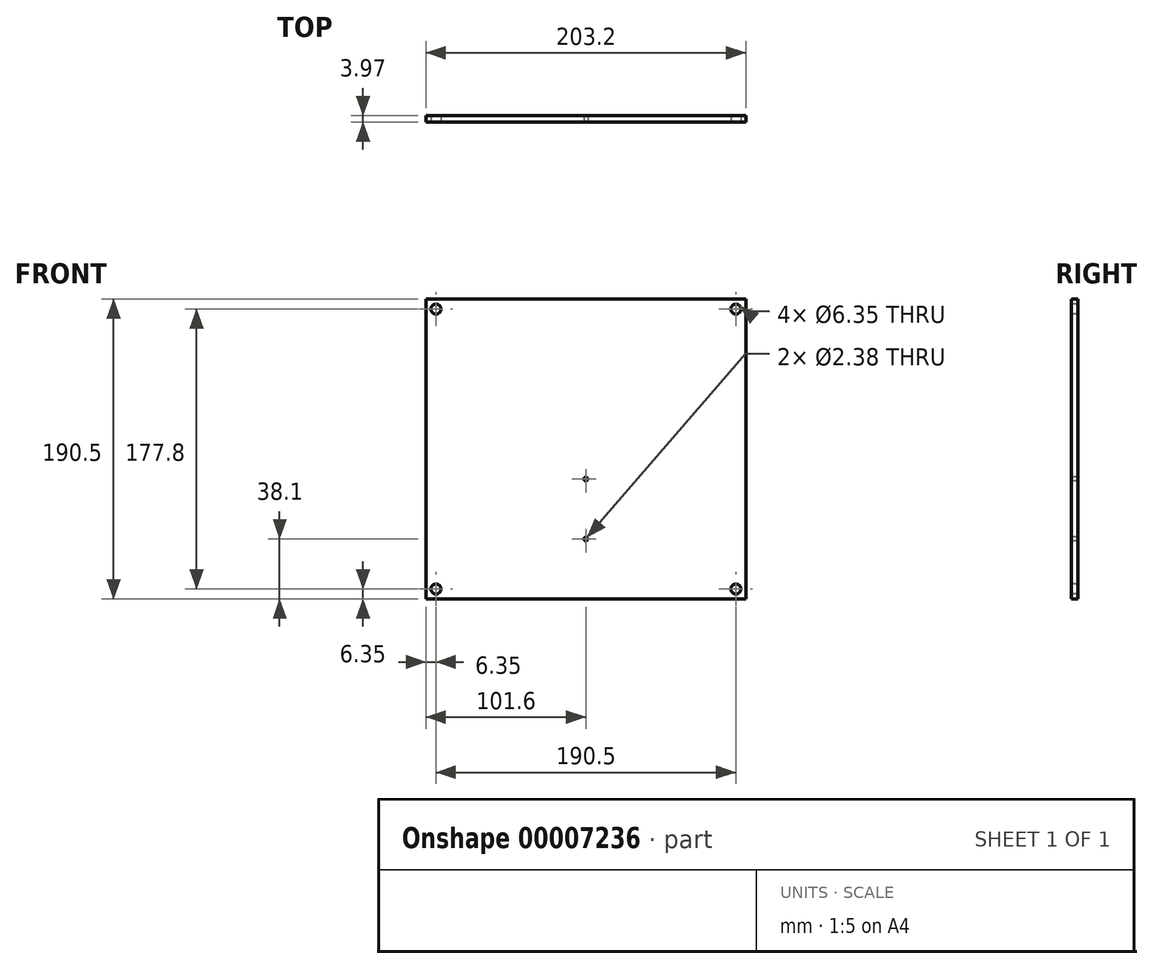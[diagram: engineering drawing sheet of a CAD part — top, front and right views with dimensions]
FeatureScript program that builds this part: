
annotation { "Feature Type Name" : "Feature", "Feature Type Description" : "" }
export const myFeature = defineFeature(function(context is Context, id is Id, definition is map)
    precondition{}
    {
        {
            var Q0;
            Q0=qCreatedBy(makeId("Front.planeOp"),FACE);
            cPlane(context, id + "F0", {"entities" : qUnion([Q0]), "cplaneType" : CPlaneType.OFFSET, "offset" : 14.29 * mm, "oppositeDirection" : true, "width" : 152.4 * mm, "height" : 152.4 * mm});
        }
        {
            var Q0;
            Q0=qCreatedBy(id+"F0.planeOp",FACE);
            var sketch = newSketch(context, id + "F1", { "sketchPlane" : qUnion([Q0])});
            skLineSegment(sketch, "E0.bottom", {"start": v(-101.6, 114.3) * mm, "end": v(101.6, 114.3) * mm});
            skLineSegment(sketch, "E0.top", {"start": v(-101.6, -76.2) * mm, "end": v(101.6, -76.2) * mm});
            skLineSegment(sketch, "E0.left", {"start": v(-101.6, 114.3) * mm, "end": v(-101.6, -76.2) * mm});
            skLineSegment(sketch, "E0.right", {"start": v(101.6, 114.3) * mm, "end": v(101.6, -76.2) * mm});
            skLineSegment(sketch, "E1", {"start": v(0, 114.3) * mm, "end": v(0, -76.2) * mm, "construction": true});
            skSolve(sketch);
        }
        {
            var Q0;
            Q0=qSketchRegion(id+"F1",true);
            extrude(context, id + "F2", {"entities" : qUnion([Q0]), "oppositeDirection" : true, "depth" : 3.97 * mm});
        }
        {
            var Q0;
            Q0=makeQuery(id+"F2.opExtrude","CAP_FACE",FACE,{"disambiguationData":[OSD([sQuery(id+"F1.wireOp",EDGE,"E0.bottom"),sQuery(id+"F1.wireOp",EDGE,"E0.top"),sQuery(id+"F1.wireOp",EDGE,"E0.left"),sQuery(id+"F1.wireOp",EDGE,"E0.right")])],"isStart":true});
            var sketch = newSketch(context, id + "F3", { "sketchPlane" : qUnion([Q0])});
            skCircle(sketch, "E2", {"center": v(-95.25, 107.95) * mm, "radius": 3.18 * mm});
            skCircle(sketch, "E3", {"center": v(95.25, 107.95) * mm, "radius": 3.18 * mm});
            skCircle(sketch, "E4", {"center": v(95.25, -69.85) * mm, "radius": 3.18 * mm});
            skCircle(sketch, "E5", {"center": v(-95.25, -69.85) * mm, "radius": 3.18 * mm});
            skSolve(sketch);
        }
        {
            var Q0;
            Q0=qSketchRegion(id+"F3",true);
            extrude(context, id + "F4", {"entities" : qUnion([Q0]), "operationType" : NewBodyOperationType.REMOVE, "endBound" : BoundingType.UP_TO_NEXT, "oppositeDirection" : true, "depth" : 25.4 * mm});
        }
        {
            var Q0;
            Q0=makeQuery(id+"F2.opExtrude","CAP_FACE",FACE,{"disambiguationData":[OSD([sQuery(id+"F1.wireOp",EDGE,"E0.bottom"),sQuery(id+"F1.wireOp",EDGE,"E0.top"),sQuery(id+"F1.wireOp",EDGE,"E0.left"),sQuery(id+"F1.wireOp",EDGE,"E0.right")])],"isStart":true});
            var sketch = newSketch(context, id + "F5", { "sketchPlane" : qUnion([Q0])});
            skCircle(sketch, "E6", {"center": v(0, 0) * mm, "radius": 1.2 * mm});
            skCircle(sketch, "E7", {"center": v(0, -38.1) * mm, "radius": 1.2 * mm});
            skSolve(sketch);
        }
        {
            var Q0;
            Q0 = qSketchRegion(id + "F5", true);
            extrude(context, id + "F6", {"entities" : qUnion([Q0]), "operationType" : NewBodyOperationType.REMOVE, "endBound" : BoundingType.THROUGH_ALL, "oppositeDirection" : true, "depth" : 25.4 * mm});
        }
    });
